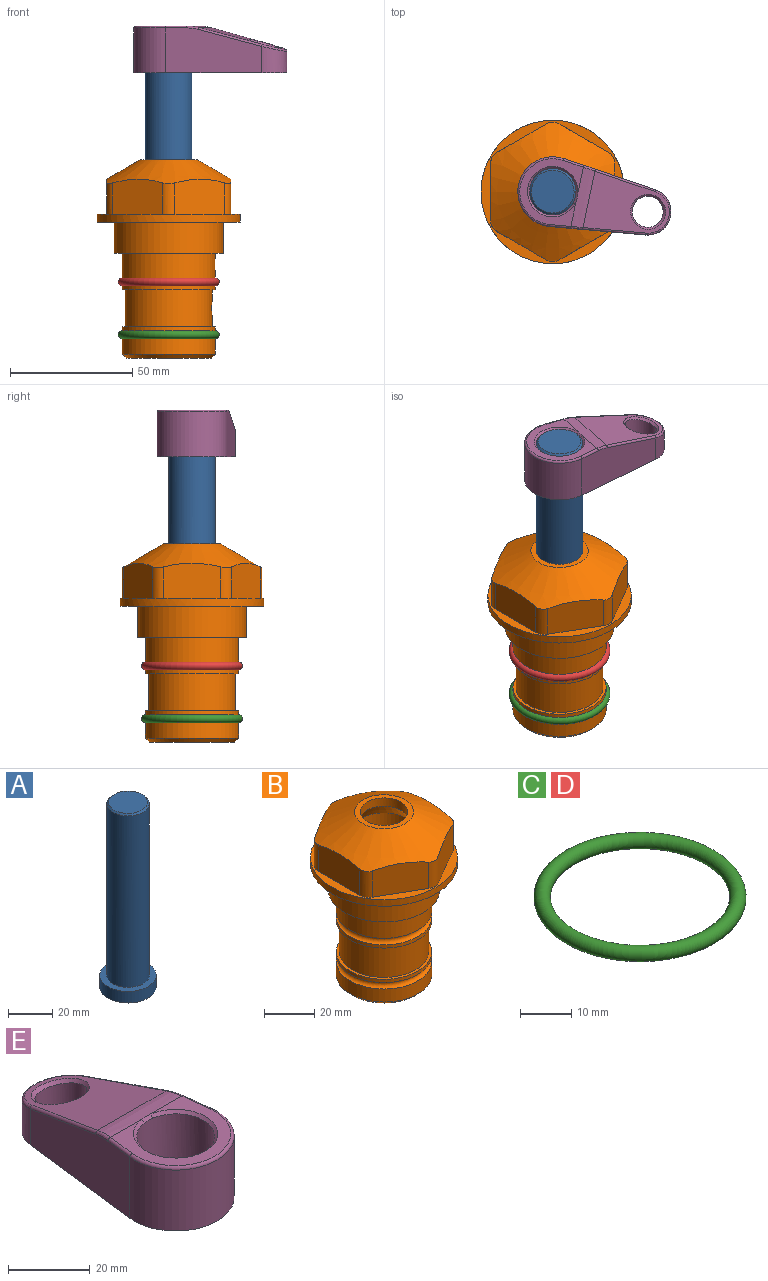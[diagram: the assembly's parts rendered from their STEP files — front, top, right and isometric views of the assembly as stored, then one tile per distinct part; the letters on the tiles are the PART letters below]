
ASSEMBLY  parts=5 mates=4
PART A: 6 faces, bbox 25.4x25.4x101.6 mm
  f0: plane 17.46x17.46mm, normal (0,0,1), area 239.5mm2, adj f5
  f1: plane 25.4x25.4mm, normal (0,0,-1), area 506.7mm2, adj f2
  f2: cylinder r=12.7mm len=25.4mm, axis (0,0,1), area 506.7mm2, adj f1,f3
  f3: plane 25.4x25.4mm, normal (0,0,1), area 221.7mm2, adj f2,f4
  f4: cylinder r=9.53mm len=94.46mm, axis (0,0,1), area 5653mm2, adj f3,f5
  f5: cone r=8.73mm half-angle=45deg, axis (0,0,-1), area 64.4mm2, adj f0,f4
PART B: 36 faces, bbox 58.7x58.7x81 mm
  f0: cylinder r=17.78mm len=35.56mm, axis (0,0,1), area 1670.8mm2, adj f23,f24,f31
  f1: cylinder r=19.05mm len=38.1mm, axis (0,0,1), area 1191.9mm2, adj f26,f27,f30
  f2: plane 58.66x58.66mm, normal (0,0,-1), area 1150.6mm2, adj f3,f28
  f3: cylinder r=29.33mm len=58.66mm, axis (0,0,-1), area 585.1mm2, adj f2,f4
  f4: plane 58.66x58.66mm, normal (0,0,1), area 475.9mm2, adj f3,f5,f6,f7,f8,f9,f10,f11
  f5: plane 20.32x14.34mm, normal (-0.5,0.87,0), area 324.4mm2, adj f4,f15,f16,f17
  f6: plane 20.32x14.34mm, normal (0.5,0.87,0), area 324.4mm2, adj f4,f14,f15,f17
  f7: plane 23.48x14.34mm, normal (1,0,0), area 324.4mm2, adj f4,f13,f14,f17
  f8: plane 20.32x14.34mm, normal (0.5,-0.87,0), area 324.4mm2, adj f4,f12,f13,f17
  f9: plane 20.32x14.34mm, normal (-0.5,-0.87,0), area 324.4mm2, adj f4,f11,f12,f17
  f10: plane 23.48x14.34mm, normal (-1,0,0), area 324.4mm2, adj f4,f11,f16,f17
  f11: cylinder r=5.08mm len=12.85mm, axis (0,0,-1), area 67.2mm2, adj f4,f9,f10,f17
  f12: cylinder r=5.08mm len=12.85mm, axis (0,0,-1), area 67.2mm2, adj f4,f8,f9,f17
  f13: cylinder r=5.08mm len=12.85mm, axis (0,0,-1), area 67.2mm2, adj f4,f7,f8,f17
  f14: cylinder r=5.08mm len=12.85mm, axis (0,0,-1), area 67.2mm2, adj f4,f6,f7,f17
  f15: cylinder r=5.08mm len=12.85mm, axis (0,0,-1), area 67.2mm2, adj f4,f5,f6,f17
  f16: cylinder r=5.08mm len=12.85mm, axis (0,0,-1), area 67.2mm2, adj f4,f5,f10,f17
  f17: cone r=11.73mm half-angle=60deg, axis (0,0,-1), area 2071.8mm2, adj f5,f6,f7,f8,f9,f10,f11,f12
  f18: plane 23.46x23.46mm, normal (0,0,1), area 147.4mm2, adj f17,f35
  f19: plane 34.93x34.93mm, normal (0,0,-1), area 958mm2, adj f29
  f20: cylinder r=19.05mm len=38.1mm, axis (0,0,1), area 760.1mm2, adj f21,f29
  f21: torus R=19.05mm, axis (0,0,1), area 565.3mm2, adj f20,f22
  f22: cylinder r=19.05mm len=38.1mm, axis (0,0,1), area 190mm2, adj f21,f23
  f23: plane 38.1x38.1mm, normal (0,0,1), area 146.9mm2, adj f0,f22
  f24: plane 38.1x38.1mm, normal (0,0,-1), area 146.9mm2, adj f0,f25
  f25: cylinder r=19.05mm len=38.1mm, axis (0,0,1), area 190mm2, adj f24,f26
  f26: torus R=19.05mm, axis (0,0,1), area 565.3mm2, adj f1,f25
  f27: plane 44.45x44.45mm, normal (0,0,-1), area 411.7mm2, adj f1,f28
  f28: cylinder r=22.23mm len=44.45mm, axis (0,0,1), area 1773.5mm2, adj f2,f27
  f29: cone r=19.05mm half-angle=45deg, axis (0,0,1), area 257.5mm2, adj f19,f20
  f30: cylinder r=3.17mm len=6.75mm, axis (-1,0,0), area 128mm2, adj f1,f33
  f31: cylinder r=3.17mm len=6.35mm, axis (-1,0,0), area 102.5mm2, adj f0,f33
  f32: plane 25.4x25.4mm, normal (0,0,1), area 506.7mm2, adj f33
  f33: cylinder r=12.7mm len=66.42mm, axis (0,0,-1), area 5236.2mm2, adj f30,f31,f32,f34
  f34: cone r=9.53mm half-angle=30deg, axis (0,0,-1), area 443.4mm2, adj f33,f35
  f35: cylinder r=9.53mm len=19.05mm, axis (0,0,-1), area 240.9mm2, adj f18,f34
PART C: 1 faces, bbox 44.7x44.7x3.2 mm
  f0: torus R=19.05mm, axis (0,0,1), area 1193.9mm2
PART D: same geometry as C
PART E: 31 faces, bbox 31.7x65.5x19.8 mm
  f0: plane 39.12x18.26mm, normal (0.99,0.12,0), area 612.2mm2, adj f1,f4,f7,f11,f13,f15
  f1: cylinder r=9.53mm len=18.91mm, axis (0,0,-1), area 296.1mm2, adj f0,f2,f7,f17
  f2: plane 39.12x18.26mm, normal (-0.99,0.12,0), area 612.2mm2, adj f1,f4,f7,f12,f14,f16
  f3: cylinder r=6.35mm len=12.7mm, axis (0,0,-1), area 362.4mm2, adj f7,f18
  f4: cylinder r=14.29mm len=28.58mm, axis (0,0,-1), area 882.2mm2, adj f0,f2,f7,f10
  f5: cylinder r=9.53mm len=19.05mm, axis (0,0,-1), area 1092.6mm2, adj f7,f19,f20
  f6: plane 26.99x23.69mm, normal (0,0,1), area 216.2mm2, adj f9,f10,f11,f12,f19
  f7: plane 63.5x28.58mm, normal (0,0,-1), area 661.8mm2, adj f0,f1,f2,f3,f4,f5,f22,f23
  f8: plane 33.52x23.6mm, normal (0,0.26,0.97), area 486mm2, adj f9,f15,f16,f17,f18
  f9: cylinder r=19.05mm len=24.72mm, axis (1,0,0), area 120.4mm2, adj f6,f8,f13,f14,f20
  f10: torus R=13.49mm, axis (0,0,1), area 59mm2, adj f4,f6,f11,f12
  f11: cylinder r=0.79mm len=8.67mm, axis (0.12,-0.99,0), area 10.8mm2, adj f0,f6,f10,f13
  f12: cylinder r=0.79mm len=8.67mm, axis (0.12,0.99,0), area 10.8mm2, adj f2,f6,f10,f14
  f13: bspline ~4.95x1.42mm, area 6.1mm2, adj f0,f9,f11,f15
  f14: bspline ~4.95x1.42mm, area 6.1mm2, adj f2,f9,f12,f16
  f15: cylinder r=0.79mm len=25.95mm, axis (0.12,-0.96,0.26), area 32.9mm2, adj f0,f8,f13,f17
  f16: cylinder r=0.79mm len=25.95mm, axis (0.12,0.96,-0.26), area 32.9mm2, adj f2,f8,f14,f17
  f17: bspline ~18.91x8.38mm, area 30mm2, adj f1,f8,f15,f16
  f18: bspline ~14.29x14.29mm, area 48.3mm2, adj f3,f8
  f19: cone r=9.53mm half-angle=45deg, axis (0,0,1), area 66.5mm2, adj f5,f6,f20
  f20: bspline ~3.22x0.96mm, area 3.5mm2, adj f5,f9,f19
  f21: plane 2.75x2.72mm, normal (0,0,-1), area 2.9mm2, adj f23,f25,f28
  f22: plane 23.05x15.88mm, normal (-0.99,-0.12,0), area 323.6mm2, adj f7,f25,f26,f27,f28,f29
  f23: plane 23.05x15.88mm, normal (0.99,-0.12,0), area 323.6mm2, adj f7,f21,f25,f27,f28,f30
  f24: cylinder r=9.53mm len=10.69mm, axis (0,0,-1), area 114.7mm2, adj f7,f27,f29,f30
  f25: cylinder r=12.7mm len=20.59mm, axis (0,0,-1), area 381.1mm2, adj f7,f21,f22,f23,f26,f28
  f26: plane 2.75x2.72mm, normal (0,0,-1), area 2.9mm2, adj f22,f25,f28
  f27: plane 19.72x18.37mm, normal (0,-0.26,-0.97), area 291.8mm2, adj f22,f23,f24,f28,f29,f30
  f28: cylinder r=15.88mm len=19.92mm, axis (1,0,0), area 54.8mm2, adj f21,f22,f23,f25,f26,f27
  f29: cylinder r=1.59mm len=11mm, axis (0,0,-1), area 34.7mm2, adj f7,f22,f24,f27
  f30: cylinder r=1.59mm len=11mm, axis (0,0,-1), area 34.7mm2, adj f7,f23,f24,f27
PLACE A rot(axis=(0,0,-1),101.9deg) t=(0,0,16.67)mm
PLACE B at identity fixed
PLACE C t=(0,0,-21.59)mm
PLACE D at identity
PLACE E rot(axis=(0,0,-1),101.9deg) t=(0,0,16.67)mm
MATE fastened C.f0 <-> B.f0  axis (0,0,1) through (0,0,-46.1)mm
MATE fastened E.f4 <-> A.f2  axis (0,0,1) through (0,0,80.17)mm
MATE fastened D.f0 <-> B.f0  axis (0,0,1) through (0,0,-24.51)mm
MATE cylindrical B.f0 <-> A.f2  axis (0,0,-1) through (0,0,21.37)mm
